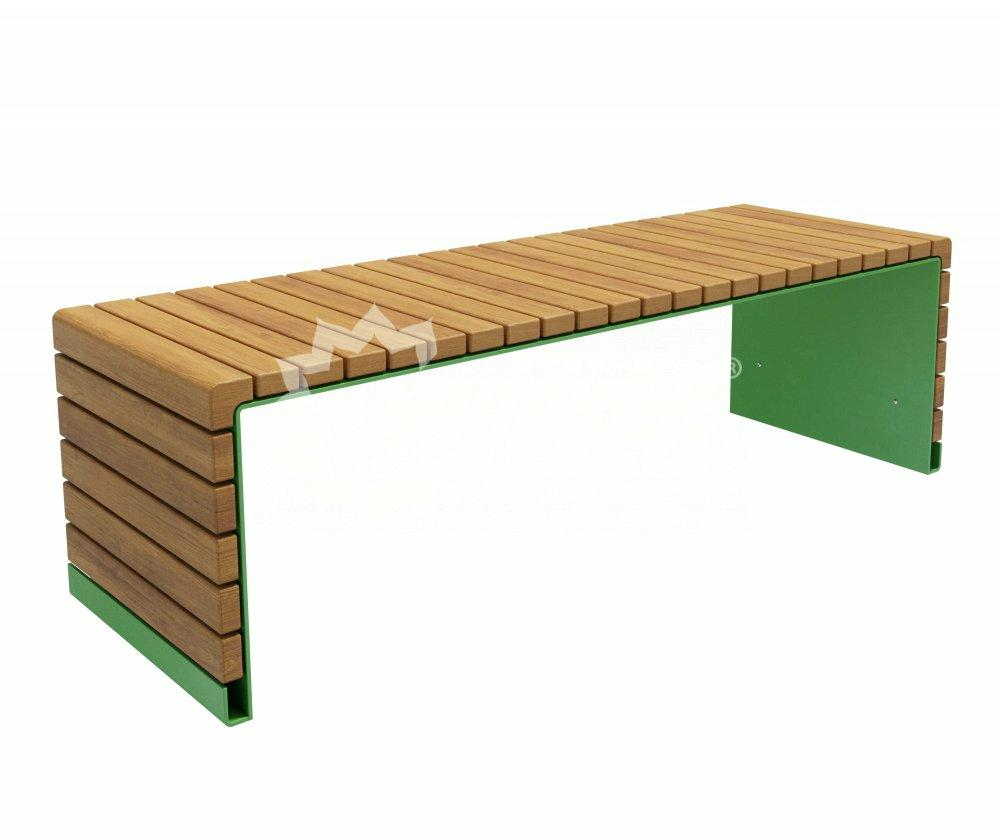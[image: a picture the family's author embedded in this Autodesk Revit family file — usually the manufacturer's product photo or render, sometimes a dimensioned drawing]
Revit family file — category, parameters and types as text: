
# Revit family: Скамейка стальная «Бракет» без спинки Арт 12984
name_source: partatom
category: Антураж
revit_build: Autodesk Revit 2018 (Build: 20180423_1000(x64)
units: mm (PartAtom-declared; Revit-internal decimal feet)

## family parameters
Всегда вертикально = Да
Источник визуального образа = Геометрия семейства
На основе рабочей плоскости = Нет
Общий = Нет
При загрузке вырезать с полостями = Нет
Точка расчета площади = Нет

## types (2) — shared parameters
URL = https://hobbyka.ru
Артикул товара = Арт. 12984
Высота = 450 мм
Группа модели = Скамейки
Изготовитель = ООО «Хоббика»
Изображение типоразмера = Скамейка стальная «Бракет» без спинки Арт 12984.jpg
Материал изделия = Сталь, дерево
Цвет лавки = Дерево
Цвет основания = Сталь
Ширина = 500 мм

## per-type parameters (varying)
| type | Версия 1,5 м | Версия 1,8 м | Длина | Описание |
| Версия 1,5 м | Да | Нет | 1500 мм | Скамейка стальная «Бракет» без спинки. Версия 1,5 м |
| Версия 1,8 м | Нет | Да | 1800 мм | Скамейка стальная «Бракет» без спинки. Версия 1,8 м |
